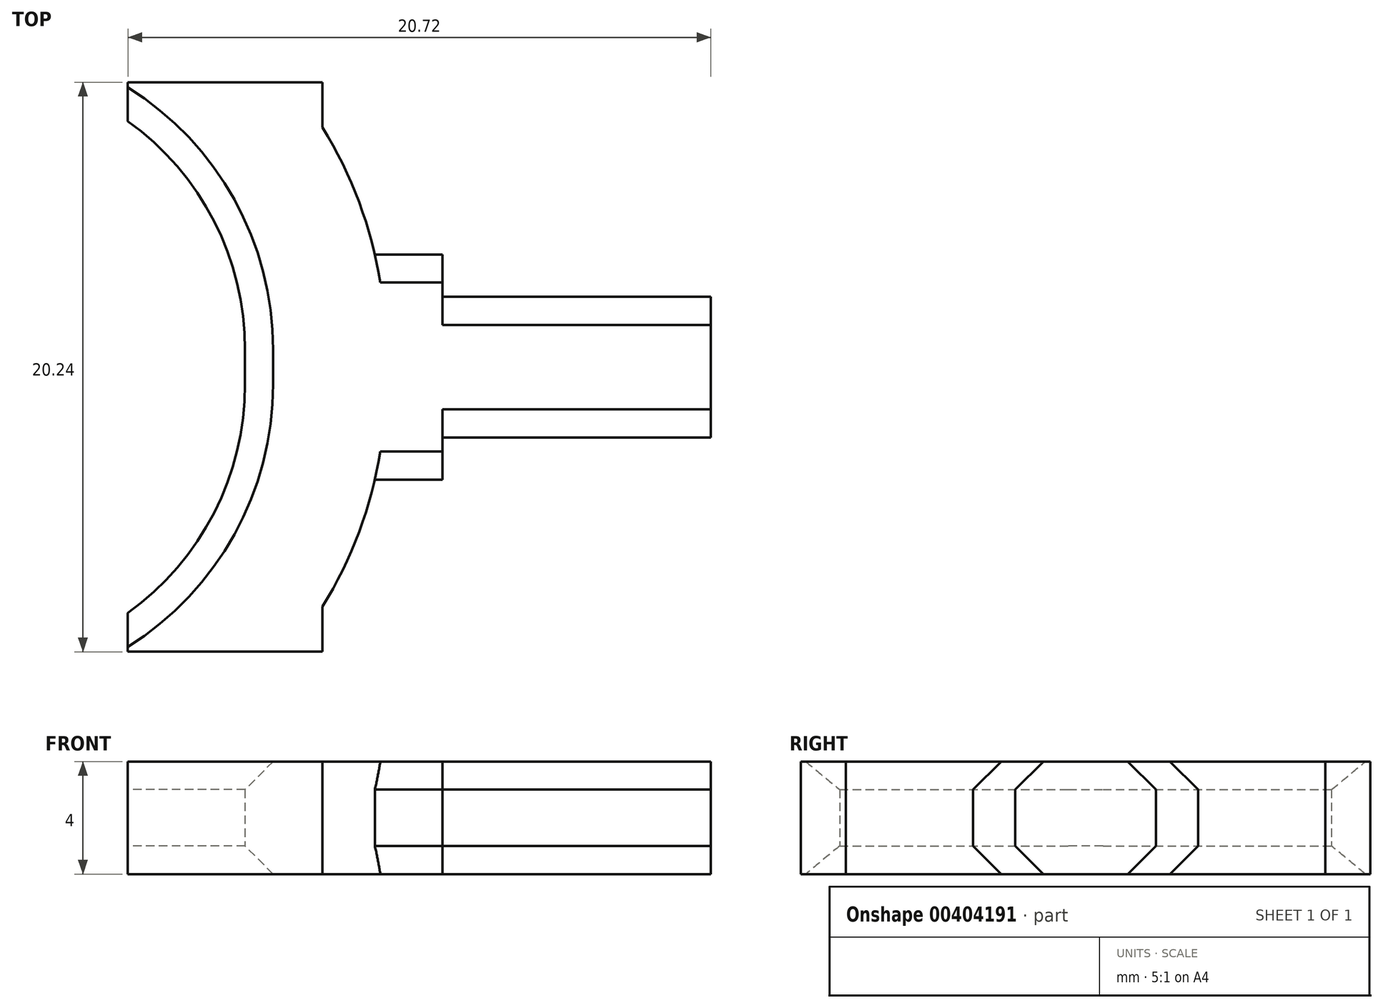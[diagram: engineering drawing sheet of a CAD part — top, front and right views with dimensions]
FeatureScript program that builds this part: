
annotation { "Feature Type Name" : "Feature", "Feature Type Description" : "" }
export const myFeature = defineFeature(function(context is Context, id is Id, definition is map)
    precondition{}
    {
        {
            var Q0;
            Q0=qCreatedBy(makeId("Top.planeOp"),FACE);
            var sketch = newSketch(context, id + "F0", { "sketchPlane" : qUnion([Q0])});
            skLineSegment(sketch, "E0", {"start": v(0, 27.49) * mm, "end": v(20, -24.82) * mm, "construction": true});
            skLineSegment(sketch, "E1", {"start": v(13, -35) * mm, "end": v(-25, -35) * mm, "construction": true});
            skLineSegment(sketch, "E2", {"start": v(-25, -35) * mm, "end": v(-26.14, -32.01) * mm, "construction": true});
            skLineSegment(sketch, "E3", {"start": v(-50, 30.38) * mm, "end": v(-76, 30.38) * mm, "construction": true});
            skLineSegment(sketch, "E4", {"start": v(-90, 44.38) * mm, "end": v(-90, 60.38) * mm, "construction": true});
            skLineSegment(sketch, "E5.bottom", {"start": v(-76, 55.62) * mm, "end": v(-70.17, 55.62) * mm, "construction": true});
            skLineSegment(sketch, "E5.top", {"start": v(-76, 34.38) * mm, "end": v(-70.17, 34.38) * mm, "construction": true});
            skLineSegment(sketch, "E5.left", {"start": v(-86, 45.62) * mm, "end": v(-86, 44.38) * mm, "construction": true});
            skLineSegment(sketch, "E5.right", {"start": v(-53.96, 45.62) * mm, "end": v(-53.96, 44.38) * mm, "construction": true});
            skPoint(sketch, "E6.visualSharp", {"position": v(-86, 55.62) * mm});
            skArc(sketch, "E6.filletArc", {"start": v(-76, 55.62) * mm, "mid": v(-83.07, 52.69) * mm, "end": v(-86, 45.62) * mm, "construction": true});
            skPoint(sketch, "E7.visualSharp", {"position": v(-86, 34.38) * mm});
            skArc(sketch, "E7.filletArc", {"start": v(-86, 44.38) * mm, "mid": v(-83.07, 37.31) * mm, "end": v(-76, 34.38) * mm, "construction": true});
            skPoint(sketch, "E8.visualSharp", {"position": v(-53.96, 34.38) * mm});
            skPoint(sketch, "E9.visualSharp", {"position": v(-53.96, 55.62) * mm});
            skPoint(sketch, "E10.visualSharp", {"position": v(-90, 30.38) * mm});
            skArc(sketch, "E10.filletArc", {"start": v(-90, 44.38) * mm, "mid": v(-85.9, 34.48) * mm, "end": v(-76, 30.38) * mm, "construction": true});
            skArc(sketch, "E11", {"start": v(-26.14, -32.01) * mm, "mid": v(-21.53, -21.68) * mm, "end": v(-31.86, -17.07) * mm, "construction": true});
            skArc(sketch, "E12", {"start": v(-33, -14.08) * mm, "mid": v(-27.23, -1.17) * mm, "end": v(-40.14, 4.6) * mm, "construction": true});
            skArc(sketch, "E13", {"start": v(-41.29, 7.6) * mm, "mid": v(-36.1, 19.21) * mm, "end": v(-47.71, 24.4) * mm, "construction": true});
            skLineSegment(sketch, "E14.trimOffspring", {"start": v(-47.71, 24.4) * mm, "end": v(-50, 30.38) * mm, "construction": true});
            skLineSegment(sketch, "E15.trimOffspring", {"start": v(-40.14, 4.6) * mm, "end": v(-41.29, 7.6) * mm, "construction": true});
            skLineSegment(sketch, "E16.trimOffspring", {"start": v(-31.86, -17.07) * mm, "end": v(-33, -14.08) * mm, "construction": true});
            skCircle(sketch, "E17", {"center": v(-5.17, -15) * mm, "radius": 2.25 * mm, "construction": true});
            skCircle(sketch, "E18", {"center": v(-23.02, 31.7) * mm, "radius": 2.25 * mm, "construction": true});
            skLineSegment(sketch, "E19", {"start": v(-78.02, 73.92) * mm, "end": v(-60.02, 73.92) * mm, "construction": true});
            skLineSegment(sketch, "E20", {"start": v(-30.61, 51.12) * mm, "end": v(-25.61, 51.12) * mm, "construction": true});
            skLineSegment(sketch, "E21", {"start": v(-25.61, 51.12) * mm, "end": v(-25.61, 52.5) * mm, "construction": true});
            skLineSegment(sketch, "E22", {"start": v(-53.96, 45) * mm, "end": v(-22.83, 45) * mm, "construction": true});
            skLineSegment(sketch, "E23.MirrorCS", {"start": v(-30.61, 38.88) * mm, "end": v(-25.61, 38.88) * mm, "construction": true});
            skLineSegment(sketch, "E24.MirrorCS", {"start": v(-25.61, 38.88) * mm, "end": v(-25.61, 37.5) * mm, "construction": true});
            skLineSegment(sketch, "E25", {"start": v(-25.61, 52.5) * mm, "end": v(-12.61, 52.5) * mm, "construction": true});
            skLineSegment(sketch, "E26.MirrorCS", {"start": v(-25.61, 37.5) * mm, "end": v(-12.61, 37.5) * mm, "construction": true});
            skLineSegment(sketch, "E27", {"start": v(-12.61, 45) * mm, "end": v(-12.61, 45) * mm});
            skPoint(sketch, "E28.end.orphan", {"position": v(-15.65, 52.5) * mm});
            skPoint(sketch, "E28.start.orphan", {"position": v(-15.65, 45.74) * mm});
            skPoint(sketch, "E29.start.orphan", {"position": v(-15.65, 43.26) * mm});
            skPoint(sketch, "E30.orphan", {"position": v(-15.65, 37.5) * mm});
            skLineSegment(sketch, "E31", {"start": v(-30.61, 51.12) * mm, "end": v(-30.61, 51.12) * mm});
            skLineSegment(sketch, "E32.MirrorCS", {"start": v(-30.61, 38.88) * mm, "end": v(-30.61, 38.88) * mm});
            skLineSegment(sketch, "E33", {"start": v(-64.33, 55.62) * mm, "end": v(-47.31, 55.62) * mm, "construction": true});
            skLineSegment(sketch, "E34", {"start": v(-30.61, 55.62) * mm, "end": v(-30.61, 51.12) * mm, "construction": true});
            skLineSegment(sketch, "E35.MirrorCS", {"start": v(-64.33, 34.38) * mm, "end": v(-47.31, 34.38) * mm, "construction": true});
            skLineSegment(sketch, "E36.MirrorCS", {"start": v(-30.61, 34.38) * mm, "end": v(-30.61, 38.88) * mm, "construction": true});
            skPoint(sketch, "E37.orphan", {"position": v(-55.65, 38.88) * mm});
            skPoint(sketch, "E38.orphan", {"position": v(-55.65, 51.12) * mm});
            skCircle(sketch, "E39", {"center": v(-67.52, 66.42) * mm, "radius": 2.25 * mm, "construction": true});
            skArc(sketch, "E40", {"start": v(13, -35) * mm, "mid": v(19.17, -31.75) * mm, "end": v(20, -24.82) * mm, "construction": true});
            skPoint(sketch, "E41.orphan", {"position": v(23.9, -35) * mm});
            skLineSegment(sketch, "E42", {"start": v(0, 27.49) * mm, "end": v(-3.83, 37.5) * mm, "construction": true});
            skLineSegment(sketch, "E43", {"start": v(-60.02, 73.92) * mm, "end": v(-60.02, 58.92) * mm, "construction": true});
            skLineSegment(sketch, "E44", {"start": v(-60.02, 58.92) * mm, "end": v(-12.02, 58.92) * mm, "construction": true});
            skPoint(sketch, "E45.start.orphan", {"position": v(-17.76, 73.92) * mm});
            skPoint(sketch, "E46.orphan", {"position": v(-31.02, 73.92) * mm});
            skArc(sketch, "E47", {"start": v(-90, 45.62) * mm, "mid": v(-88.7, 51.5) * mm, "end": v(-85.07, 56.28) * mm, "construction": true});
            skLineSegment(sketch, "E48", {"start": v(-78.02, 73.92) * mm, "end": v(-78.02, 71.52) * mm, "construction": true});
            skArc(sketch, "E49", {"start": v(-85.07, 56.28) * mm, "mid": v(-79.87, 63.13) * mm, "end": v(-78.02, 71.52) * mm, "construction": true});
            skLineSegment(sketch, "E50", {"start": v(-60.02, 58.92) * mm, "end": v(-82.49, 58.92) * mm, "construction": true});
            skLineSegment(sketch, "E51", {"start": v(-60.02, 73.92) * mm, "end": v(-17.76, 73.92) * mm, "construction": true});
            skLineSegment(sketch, "E52", {"start": v(-12.02, 58.92) * mm, "end": v(-12.02, 73.92) * mm, "construction": true});
            skLineSegment(sketch, "E53", {"start": v(-12.02, 73.92) * mm, "end": v(-17.76, 73.92) * mm, "construction": true});
            skCircle(sketch, "E54", {"center": v(-30.02, 66.42) * mm, "radius": 2.25 * mm, "construction": true});
            skCircle(sketch, "E55", {"center": v(-50.02, 66.42) * mm, "radius": 2.25 * mm, "construction": true});
            skArc(sketch, "E56", {"start": v(-64.33, 55.62) * mm, "mid": v(-57.26, 52.69) * mm, "end": v(-54.33, 45.62) * mm, "construction": true});
            skArc(sketch, "E57", {"start": v(-64.33, 34.38) * mm, "mid": v(-57.26, 37.31) * mm, "end": v(-54.33, 44.38) * mm, "construction": true});
            skLineSegment(sketch, "E58", {"start": v(-54.33, 45.62) * mm, "end": v(-54.33, 44.38) * mm, "construction": true});
            skLineSegment(sketch, "E59", {"start": v(-9.56, 52.5) * mm, "end": v(-12.61, 52.5) * mm, "construction": true});
            skLineSegment(sketch, "E60", {"start": v(-3.83, 37.5) * mm, "end": v(-12.61, 37.5) * mm, "construction": true});
            skLineSegment(sketch, "E61.trimOffspring", {"start": v(-9.56, 52.5) * mm, "end": v(-12.02, 58.92) * mm, "construction": true});
            skLineSegment(sketch, "E62", {"start": v(-43.61, 55.62) * mm, "end": v(-43.61, 34.38) * mm, "construction": true});
            skLineSegment(sketch, "E63", {"start": v(-44.11, 55.62) * mm, "end": v(-44.11, 48.2) * mm, "construction": true});
            skLineSegment(sketch, "E64", {"start": v(-44.11, 48.2) * mm, "end": v(-47.31, 48.2) * mm, "construction": true});
            skLineSegment(sketch, "E65", {"start": v(-47.31, 48.2) * mm, "end": v(-47.31, 55.62) * mm, "construction": true});
            skLineSegment(sketch, "E66.MirrorCS", {"start": v(-44.11, 41.8) * mm, "end": v(-47.31, 41.8) * mm, "construction": true});
            skLineSegment(sketch, "E67.MirrorCS", {"start": v(-44.11, 34.38) * mm, "end": v(-44.11, 41.8) * mm, "construction": true});
            skLineSegment(sketch, "E68.MirrorCS", {"start": v(-47.31, 41.8) * mm, "end": v(-47.31, 34.38) * mm, "construction": true});
            skLineSegment(sketch, "E69.trimOffspring", {"start": v(-44.11, 55.62) * mm, "end": v(-30.61, 55.62) * mm, "construction": true});
            skLineSegment(sketch, "E70.trimOffspring", {"start": v(-44.11, 34.38) * mm, "end": v(-30.61, 34.38) * mm, "construction": true});
            skArc(sketch, "E71", {"start": v(-70.17, 34.38) * mm, "mid": v(-67.1, 34.86) * mm, "end": v(-64.33, 36.26) * mm, "construction": true});
            skLineSegment(sketch, "E72", {"start": v(-64.33, 36.26) * mm, "end": v(-64.33, 34.38) * mm, "construction": true});
            skLineSegment(sketch, "E73.MirrorCS", {"start": v(-64.33, 53.74) * mm, "end": v(-64.33, 55.62) * mm, "construction": true});
            skArc(sketch, "E74.MirrorCS", {"start": v(-70.17, 55.62) * mm, "mid": v(-67.1, 55.14) * mm, "end": v(-64.33, 53.74) * mm, "construction": true});
            skLineSegment(sketch, "E75", {"start": v(-64.33, 34.88) * mm, "end": v(-64.33, 36.26) * mm});
            skLineSegment(sketch, "E76", {"start": v(-64.33, 34.88) * mm, "end": v(-57.42, 34.88) * mm});
            skArc(sketch, "E77", {"start": v(-64.33, 36.26) * mm, "mid": v(-61.27, 39.82) * mm, "end": v(-60.17, 44.38) * mm});
            skArc(sketch, "E78", {"start": v(-64.33, 53.74) * mm, "mid": v(-61.27, 50.18) * mm, "end": v(-60.17, 45.62) * mm});
            skLineSegment(sketch, "E79.MirrorCS", {"start": v(-64.33, 55.12) * mm, "end": v(-57.42, 55.12) * mm});
            skLineSegment(sketch, "E80.MirrorCS", {"start": v(-64.33, 55.12) * mm, "end": v(-64.33, 53.74) * mm});
            skLineSegment(sketch, "E81", {"start": v(-60.17, 45.62) * mm, "end": v(-60.17, 44.38) * mm});
            skLineSegment(sketch, "E82", {"start": v(-57.42, 34.88) * mm, "end": v(-57.42, 36.48) * mm});
            skArc(sketch, "E83", {"start": v(-57.42, 36.48) * mm, "mid": v(-56.3, 38.67) * mm, "end": v(-55.55, 41) * mm});
            skLineSegment(sketch, "E84", {"start": v(-55.55, 41) * mm, "end": v(-53.15, 41) * mm});
            skLineSegment(sketch, "E85", {"start": v(-53.15, 41) * mm, "end": v(-53.15, 42.5) * mm});
            skLineSegment(sketch, "E86", {"start": v(-53.15, 42.5) * mm, "end": v(-43.61, 42.5) * mm});
            skLineSegment(sketch, "E87", {"start": v(-43.61, 42.5) * mm, "end": v(-43.61, 45) * mm});
            skLineSegment(sketch, "E88.MirrorCS", {"start": v(-57.42, 55.12) * mm, "end": v(-57.42, 53.52) * mm});
            skArc(sketch, "E89.MirrorCS", {"start": v(-57.42, 53.52) * mm, "mid": v(-56.3, 51.33) * mm, "end": v(-55.55, 49) * mm});
            skLineSegment(sketch, "E90.MirrorCS", {"start": v(-55.55, 49) * mm, "end": v(-53.15, 49) * mm});
            skLineSegment(sketch, "E91.MirrorCS", {"start": v(-53.15, 49) * mm, "end": v(-53.15, 47.5) * mm});
            skLineSegment(sketch, "E92.MirrorCS", {"start": v(-53.15, 47.5) * mm, "end": v(-43.61, 47.5) * mm});
            skLineSegment(sketch, "E93.MirrorCS", {"start": v(-43.61, 47.5) * mm, "end": v(-43.61, 45) * mm});
            skSolve(sketch);
        }
        {
            var Q0;
            Q0=qSketchRegion(id+"F0",true);
            extrude(context, id + "F1", {"entities" : qUnion([Q0]), "endBound" : BoundingType.SYMMETRIC, "depth" : 4 * mm});
        }
        {
            var Q0;
            Q0=makeQuery(id+"F1.opExtrude","CAP_EDGE",EDGE,{"disambiguationData":[OSD([sQuery(id+"F0.wireOp",EDGE,"E90.MirrorCS")])],"isStart":true});
            var Q1;
            Q1=makeQuery(id+"F1.opExtrude","CAP_EDGE",EDGE,{"disambiguationData":[OSD([sQuery(id+"F0.wireOp",EDGE,"E90.MirrorCS")])],"isStart":false});
            var Q2;
            Q2=makeQuery(id+"F1.opExtrude","CAP_EDGE",EDGE,{"disambiguationData":[OSD([sQuery(id+"F0.wireOp",EDGE,"E84")])],"isStart":false});
            var Q3;
            Q3=makeQuery(id+"F1.opExtrude","CAP_EDGE",EDGE,{"disambiguationData":[OSD([sQuery(id+"F0.wireOp",EDGE,"E84")])],"isStart":true});
            var Q4;
            Q4=makeQuery(id+"F1.opExtrude","CAP_EDGE",EDGE,{"disambiguationData":[OSD([sQuery(id+"F0.wireOp",EDGE,"E92.MirrorCS")])],"isStart":true});
            var Q5;
            Q5=makeQuery(id+"F1.opExtrude","CAP_EDGE",EDGE,{"disambiguationData":[OSD([sQuery(id+"F0.wireOp",EDGE,"E86")])],"isStart":true});
            var Q6;
            Q6=makeQuery(id+"F1.opExtrude","CAP_EDGE",EDGE,{"disambiguationData":[OSD([sQuery(id+"F0.wireOp",EDGE,"E92.MirrorCS")])],"isStart":false});
            var Q7;
            Q7=makeQuery(id+"F1.opExtrude","CAP_EDGE",EDGE,{"disambiguationData":[OSD([sQuery(id+"F0.wireOp",EDGE,"E86")])],"isStart":false});
            var Q8;
            Q8=makeQuery(id+"F1.opExtrude","CAP_EDGE",EDGE,{"disambiguationData":[OSD([sQuery(id+"F0.wireOp",EDGE,"E78")])],"isStart":false});
            var Q9;
            Q9=makeQuery(id+"F1.opExtrude","CAP_EDGE",EDGE,{"disambiguationData":[OSD([sQuery(id+"F0.wireOp",EDGE,"E77")])],"isStart":true});
            var Q10;
            Q10=makeQuery(id+"F71yMvw25n6rzc8_1.boolean.opBoolean","COPY",EDGE,{"derivedFrom":makeQuery(id+"F71yMvw25n6rzc8_1.opExtrude","SWEPT_EDGE",EDGE,{"disambiguationData":[OSD([sQuery(id+"F0.wireOp",EDGE,"E85"),sQuery(id+"F0.wireOp",EDGE,"E86"),sQuery(id+"FfKaAA7rpaZFhOo_1.wireOp",EDGE,"0pxokbgW-zWwp-ka6L-d4TH-zkUkQvHXfEjo.top"),sQuery(id+"FfKaAA7rpaZFhOo_1.wireOp",EDGE,"FnZmNtwL-1kKO-QJeP-jnQv-RpB50fH07GHO")])]})});
            var Q11;
            Q11=makeQuery(id+"F71yMvw25n6rzc8_1.boolean.opBoolean","COPY",EDGE,{"derivedFrom":makeQuery(id+"F71yMvw25n6rzc8_1.opExtrude","SWEPT_EDGE",EDGE,{"disambiguationData":[OSD([sQuery(id+"FfKaAA7rpaZFhOo_1.wireOp",EDGE,"0pxokbgW-zWwp-ka6L-d4TH-zkUkQvHXfEjo.top"),sQuery(id+"FfKaAA7rpaZFhOo_1.wireOp",EDGE,"Df0fTSdf-QTTZ-zjBM-0rUB-91WAqwvci8P1")])]})});
            chamfer(context, id + "F2", {"entities" : qUnion([Q0, Q1, Q2, Q3, Q4, Q5, Q6, Q7, Q8, Q9, Q10, Q11]), "width" : 1 * mm, "tangentPropagation" : true});
        }
    });
